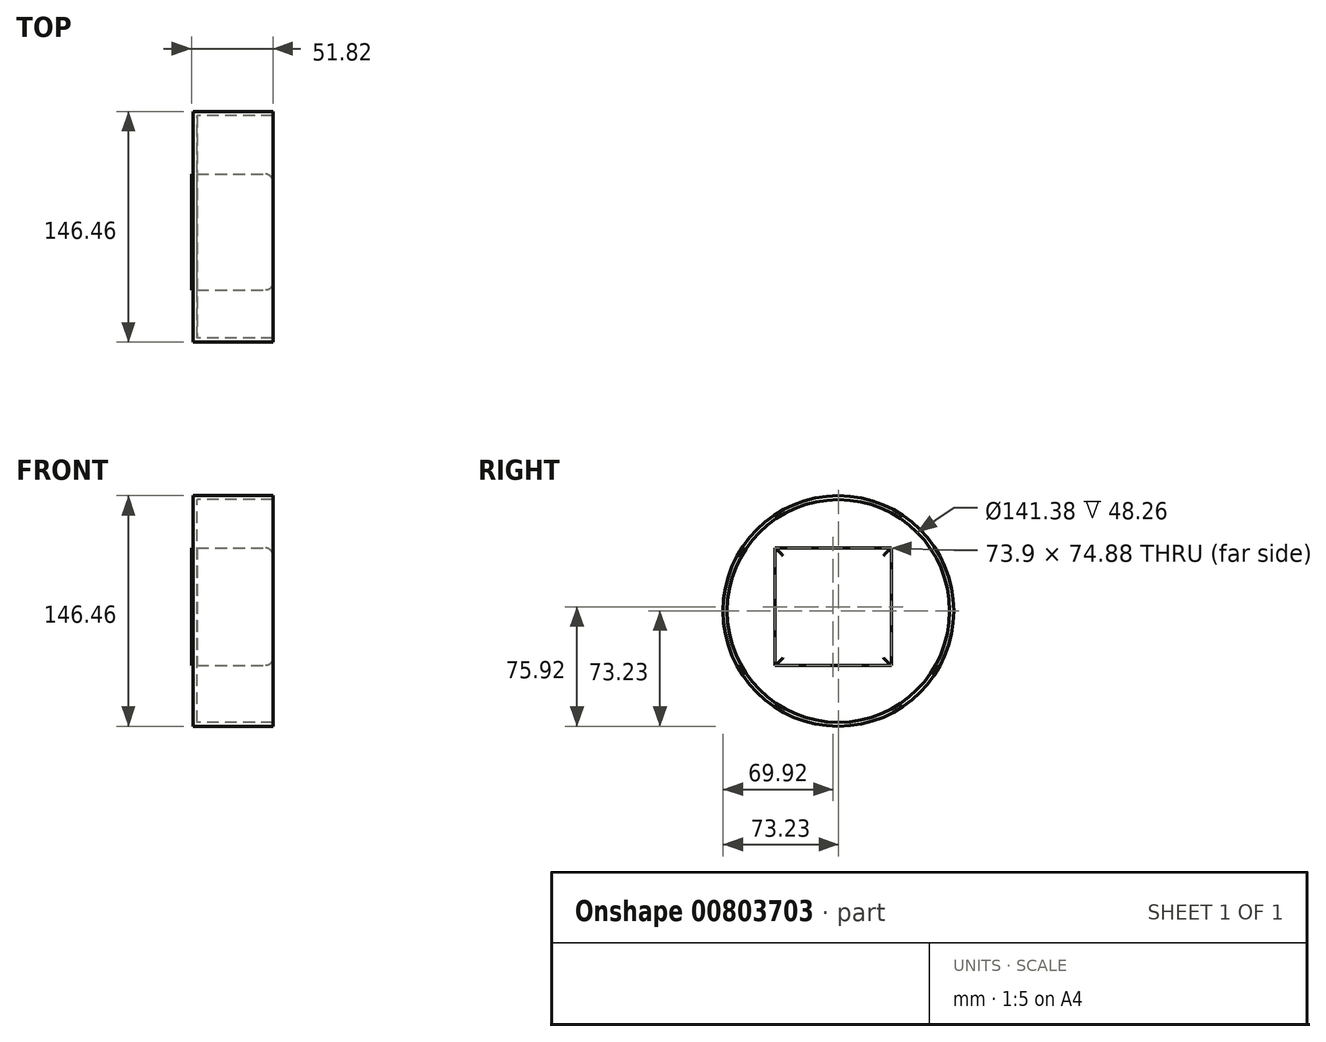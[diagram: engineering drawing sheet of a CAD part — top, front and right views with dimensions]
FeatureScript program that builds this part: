
annotation { "Feature Type Name" : "Feature", "Feature Type Description" : "" }
export const myFeature = defineFeature(function(context is Context, id is Id, definition is map)
    precondition{}
    {
        {
            var Q0;
            Q0=qCreatedBy(makeId("Right.planeOp"),FACE);
            var sketch = newSketch(context, id + "F0", { "sketchPlane" : qUnion([Q0])});
            skCircle(sketch, "E0", {"center": v(0, 0) * mm, "radius": 73.23 * mm});
            skSolve(sketch);
        }
        {
            var Q0;
            Q0 = qSketchRegion(id + "F0", true);
            extrude(context, id + "F1", {"entities" : qUnion([Q0]), "depth" : 25.4 * mm, "offsetDistance" : 25.4 * mm});
        }
        {
            var Q0;
            Q0=makeQuery(id+"F1.opExtrude","CAP_FACE",FACE,{"disambiguationData":[OSD([sQuery(id+"F0.wireOp",EDGE,"E0")])],"isStart":false});
            extrude(context, id + "F2", {"entities" : qUnion([Q0]), "operationType" : NewBodyOperationType.ADD, "depth" : 25.4 * mm, "offsetDistance" : 25.4 * mm});
        }
        {
            var Q0;
            Q0=makeQuery(id+"F2.opExtrude","CAP_FACE",FACE,{"disambiguationData":[OSD([sQuery(id+"F0.wireOp",EDGE,"E0")])],"isStart":false});
            var sketch = newSketch(context, id + "F3", { "sketchPlane" : qUnion([Q0])});
            skLineSegment(sketch, "E1.bottom", {"start": v(-40.26, 40.13) * mm, "end": v(33.64, 40.13) * mm});
            skLineSegment(sketch, "E1.top", {"start": v(-40.26, -34.75) * mm, "end": v(33.64, -34.75) * mm});
            skLineSegment(sketch, "E1.left", {"start": v(-40.26, 40.13) * mm, "end": v(-40.26, -34.75) * mm});
            skLineSegment(sketch, "E1.right", {"start": v(33.64, 40.13) * mm, "end": v(33.64, -34.75) * mm});
            skSolve(sketch);
        }
        {
            var Q0;
            Q0=makeQuery(id+"F2.opExtrude","CAP_FACE",FACE,{"disambiguationData":[OSD([sQuery(id+"F0.wireOp",EDGE,"E0")])],"isStart":false});
            shell(context, id + "F4", {"entities" : qUnion([Q0]), "thickness" : 2.54 * mm});
        }
        {
            var Q0;
            Q0=makeQuery(id+"F3.imprint","IMPRINT",FACE,{"disambiguationData":[TD([[makeQuery(id+"F3.imprint","IMPRINT",EDGE,{"derivedFrom":sQuery(id+"F3.wireOp",EDGE,"E1.bottom")}),-1.0]])]});
            extrude(context, id + "F5", {"entities" : qUnion([Q0]), "operationType" : NewBodyOperationType.ADD, "oppositeDirection" : true, "depth" : 51.82 * mm, "offsetDistance" : 25.4 * mm});
        }
        {
            var Q0;
            Q0=makeQuery(id+"F5.opExtrude","CAP_EDGE",EDGE,{"disambiguationData":[OSD([sQuery(id+"F3.wireOp",EDGE,"E1.bottom")])],"isStart":true});
            var Q1;
            Q1=makeQuery(id+"F5.opExtrude","CAP_EDGE",EDGE,{"disambiguationData":[OSD([sQuery(id+"F3.wireOp",EDGE,"E1.left")])],"isStart":true});
            var Q2;
            Q2=makeQuery(id+"F5.opExtrude","CAP_EDGE",EDGE,{"disambiguationData":[OSD([sQuery(id+"F3.wireOp",EDGE,"E1.right")])],"isStart":true});
            var Q3;
            Q3=makeQuery(id+"F5.opExtrude","CAP_EDGE",EDGE,{"disambiguationData":[OSD([sQuery(id+"F3.wireOp",EDGE,"E1.top")])],"isStart":true});
            fillet(context, id + "F6", {"entities" : qUnion([Q0, Q1, Q2, Q3]), "radius" : 5.08 * mm, "tangentPropagation" : true, "allowEdgeOverflow" : false});
        }
    });
